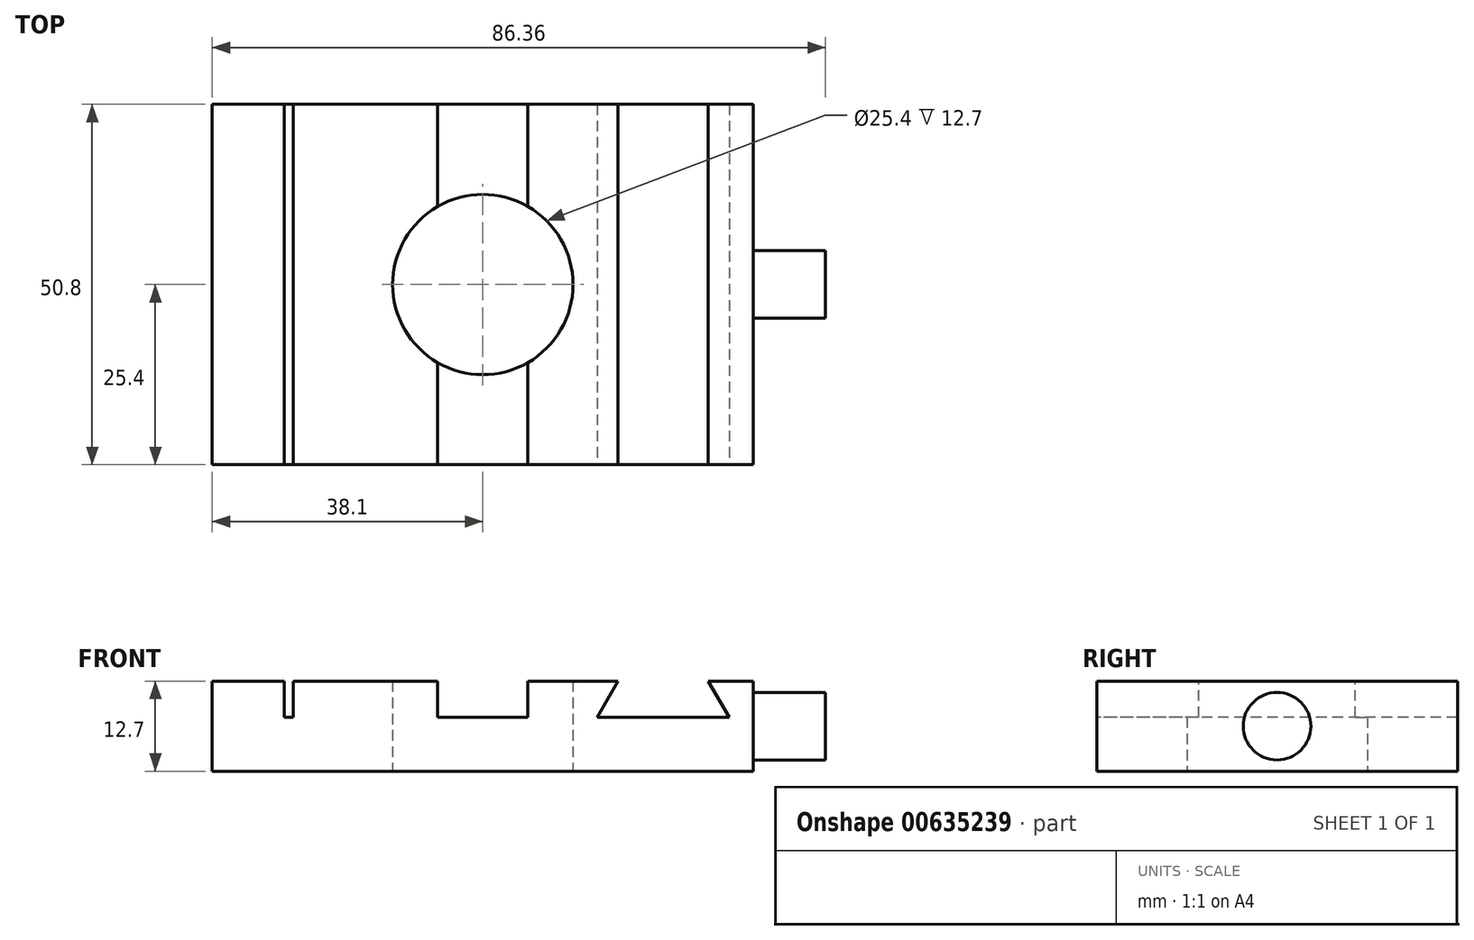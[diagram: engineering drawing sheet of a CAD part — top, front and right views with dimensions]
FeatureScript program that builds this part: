
annotation { "Feature Type Name" : "Feature", "Feature Type Description" : "" }
export const myFeature = defineFeature(function(context is Context, id is Id, definition is map)
    precondition{}
    {
        {
            var Q0;
            Q0=qCreatedBy(makeId("Top.planeOp"),FACE);
            var sketch = newSketch(context, id + "F0", { "sketchPlane" : qUnion([Q0])});
            skLineSegment(sketch, "E0.bottom", {"start": v(38.1, 25.4) * mm, "end": v(-38.1, 25.4) * mm});
            skLineSegment(sketch, "E0.top", {"start": v(38.1, -25.4) * mm, "end": v(-38.1, -25.4) * mm});
            skLineSegment(sketch, "E0.left", {"start": v(38.1, 25.4) * mm, "end": v(38.1, -25.4) * mm});
            skLineSegment(sketch, "E0.right", {"start": v(-38.1, 25.4) * mm, "end": v(-38.1, -25.4) * mm});
            skPoint(sketch, "E0.middle", {"position": v(0, 0) * mm});
            skCircle(sketch, "E1", {"center": v(0, 0) * mm, "radius": 12.7 * mm});
            skSolve(sketch);
        }
        {
            var Q0;
            Q0=makeQuery(id+"F0.imprint","IMPRINT",FACE,{"disambiguationData":[TD([[makeQuery(id+"F0.imprint","IMPRINT",EDGE,{"derivedFrom":sQuery(id+"F0.wireOp",EDGE,"E0.bottom")}),1.0]])]});
            extrude(context, id + "F1", {"entities" : qUnion([Q0]), "depth" : 12.7 * mm, "offsetDistance" : 25.4 * mm});
        }
        {
            var Q0;
            Q0=makeQuery(id+"F1.opExtrude","CAP_FACE",FACE,{"disambiguationData":[OSD([sQuery(id+"F0.wireOp",EDGE,"E0.bottom"),sQuery(id+"F0.wireOp",EDGE,"E0.top"),sQuery(id+"F0.wireOp",EDGE,"E0.left"),sQuery(id+"F0.wireOp",EDGE,"E0.right"),sQuery(id+"F0.wireOp",EDGE,"E1")])],"isStart":false});
            var sketch = newSketch(context, id + "F2", { "sketchPlane" : qUnion([Q0])});
            skLineSegment(sketch, "E2.bottom", {"start": v(-27.94, 25.4) * mm, "end": v(-26.67, 25.4) * mm});
            skLineSegment(sketch, "E2.top", {"start": v(-27.94, -25.4) * mm, "end": v(-26.67, -25.4) * mm});
            skLineSegment(sketch, "E2.left", {"start": v(-27.94, 25.4) * mm, "end": v(-27.94, -25.4) * mm});
            skLineSegment(sketch, "E2.right", {"start": v(-26.67, 25.4) * mm, "end": v(-26.67, -25.4) * mm});
            skLineSegment(sketch, "E3", {"start": v(-6.35, 25.4) * mm, "end": v(-6.35, -25.4) * mm});
            skLineSegment(sketch, "E4", {"start": v(-6.35, -25.4) * mm, "end": v(6.35, -25.4) * mm});
            skLineSegment(sketch, "E5", {"start": v(6.35, -25.4) * mm, "end": v(6.35, 25.4) * mm});
            skPoint(sketch, "E6", {"position": v(0, 0) * mm});
            skPoint(sketch, "E7.end.orphan", {"position": v(0, -25.4) * mm});
            skPoint(sketch, "E8.orphan", {"position": v(-6.35, 0) * mm});
            skPoint(sketch, "E9.start.orphan", {"position": v(6.35, 0) * mm});
            skSolve(sketch);
        }
        {
            var Q0;
            Q0=makeQuery(id+"F2.imprint","IMPRINT",FACE,{"disambiguationData":[TD([[makeQuery(id+"F2.imprint","IMPRINT",EDGE,{"derivedFrom":sQuery(id+"F2.wireOp",EDGE,"E2.bottom")}),1.0]])]});
            var Q1;
            {var subQ0=sQuery(id+"F2.wireOp",EDGE,"E3");var subQ1=makeQuery(id+"F1.opExtrude","CAP_EDGE",EDGE,{"disambiguationData":[OSD([sQuery(id+"F0.wireOp",EDGE,"E0.bottom")])],"isStart":false});var subQ2=makeQuery(id+"F2.imprint","INTERSECT",VERTEX,{"derivedFrom":[subQ1,subQ0]});Q1=makeQuery(id+"F2.imprint","IMPRINT",FACE,{"disambiguationData":[TD([[makeQuery(id+"F2.imprint","IMPRINT",EDGE,{"disambiguationData":[TD([[subQ2,-1.0]])],"derivedFrom":subQ0}),1.0]])]});}
            var Q2;
            {var subQ0=sQuery(id+"F2.wireOp",EDGE,"E4");Q2=makeQuery(id+"F2.imprint","IMPRINT",FACE,{"disambiguationData":[TD([[makeQuery(id+"F2.imprint","IMPRINT",EDGE,{"derivedFrom":subQ0}),-1.0]])]});}
            extrude(context, id + "F3", {"entities" : qUnion([Q0, Q1, Q2]), "operationType" : NewBodyOperationType.REMOVE, "oppositeDirection" : true, "depth" : 5.08 * mm, "offsetDistance" : 25.4 * mm});
        }
        {
            var Q0;
            Q0=makeQuery(id+"F1.opExtrude","SWEPT_FACE",FACE,{"disambiguationData":[OSD([sQuery(id+"F0.wireOp",EDGE,"E0.top")])]});
            var sketch = newSketch(context, id + "F4", { "sketchPlane" : qUnion([Q0])});
            skLineSegment(sketch, "E10", {"start": v(19.05, 12.7) * mm, "end": v(16.12, 7.62) * mm});
            skLineSegment(sketch, "E11", {"start": v(16.12, 7.62) * mm, "end": v(34.68, 7.62) * mm});
            skLineSegment(sketch, "E12", {"start": v(34.68, 7.62) * mm, "end": v(31.75, 12.7) * mm});
            skLineSegment(sketch, "E13", {"start": v(31.75, 12.7) * mm, "end": v(19.05, 12.7) * mm});
            skLineSegment(sketch, "E14", {"start": v(25.4, 7.62) * mm, "end": v(25.4, 12.7) * mm, "construction": true});
            skSolve(sketch);
        }
        {
            var Q0;
            Q0 = qSketchRegion(id + "F4", true);
            extrude(context, id + "F5", {"entities" : qUnion([Q0]), "operationType" : NewBodyOperationType.REMOVE, "endBound" : BoundingType.THROUGH_ALL, "oppositeDirection" : true, "depth" : 25.4 * mm, "offsetDistance" : 25.4 * mm});
        }
        {
            var Q0;
            Q0=makeQuery(id+"F1.opExtrude","SWEPT_FACE",FACE,{"disambiguationData":[OSD([sQuery(id+"F0.wireOp",EDGE,"E0.left")])]});
            var sketch = newSketch(context, id + "F6", { "sketchPlane" : qUnion([Q0])});
            skCircle(sketch, "E15", {"center": v(0, 6.35) * mm, "radius": 4.76 * mm});
            skPoint(sketch, "E15.centerSnap0", {"position": v(-25.4, 6.35) * mm});
            skPoint(sketch, "E15.centerSnap1", {"position": v(0, 12.7) * mm});
            skSolve(sketch);
        }
        {
            var Q0;
            Q0 = qSketchRegion(id + "F6", true);
            extrude(context, id + "F7", {"entities" : qUnion([Q0]), "operationType" : NewBodyOperationType.ADD, "depth" : 10.16 * mm, "offsetDistance" : 25.4 * mm});
        }
    });
